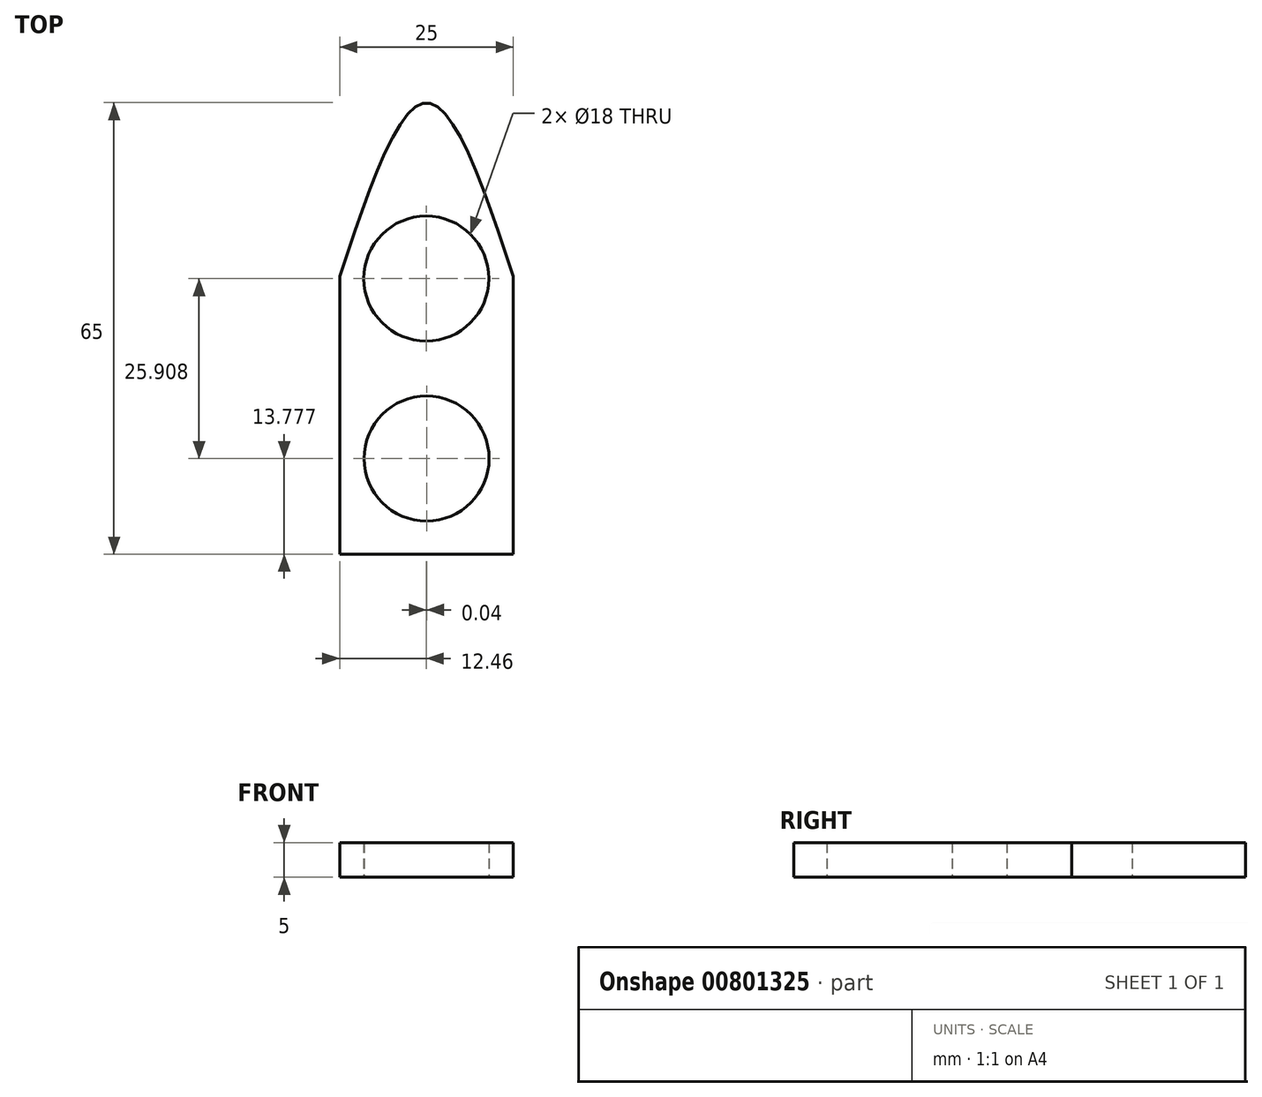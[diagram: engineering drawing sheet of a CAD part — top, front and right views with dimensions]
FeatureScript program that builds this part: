
annotation { "Feature Type Name" : "Feature", "Feature Type Description" : "" }
export const myFeature = defineFeature(function(context is Context, id is Id, definition is map)
    precondition{}
    {
        {
            var Q0;
            Q0=qCreatedBy(makeId("Top.planeOp"),FACE);
            var sketch = newSketch(context, id + "F0", { "sketchPlane" : qUnion([Q0])});
            skLineSegment(sketch, "E0", {"start": v(0, 0) * mm, "end": v(0, 65) * mm, "construction": true});
            skLineSegment(sketch, "E1", {"start": v(0, 0) * mm, "end": v(12.5, 0) * mm});
            skLineSegment(sketch, "E2", {"start": v(0, 0) * mm, "end": v(-12.5, 0) * mm});
            skLineSegment(sketch, "E3", {"start": v(12.5, 0) * mm, "end": v(12.5, 40) * mm});
            skPoint(sketch, "E4.orphan", {"position": v(-12.5, 117.44) * mm});
            skLineSegment(sketch, "E5", {"start": v(-12.5, 0) * mm, "end": v(-12.5, 40) * mm});
            skFitSpline(sketch, "E6", {"points": [v(-12.5, 40) * mm, v(0, 65) * mm, v(12.5, 40) * mm], "startDerivative": vector(25, 75) * mm, "endDerivative": vector(25, -75) * mm});
            skCircle(sketch, "E7", {"center": v(-0.04, 39.68) * mm, "radius": 9 * mm});
            skCircle(sketch, "E8", {"center": v(0, 13.78) * mm, "radius": 9 * mm});
            skSolve(sketch);
        }
        {
            var Q0;
            Q0=makeQuery(id+"F0.imprint","IMPRINT",FACE,{"disambiguationData":[TD([[makeQuery(id+"F0.imprint","IMPRINT",EDGE,{"derivedFrom":sQuery(id+"F0.wireOp",EDGE,"E1")}),1.0]])]});
            extrude(context, id + "F1", {"entities" : qUnion([Q0]), "depth" : 5 * mm, "offsetDistance" : 25 * mm});
        }
    });
